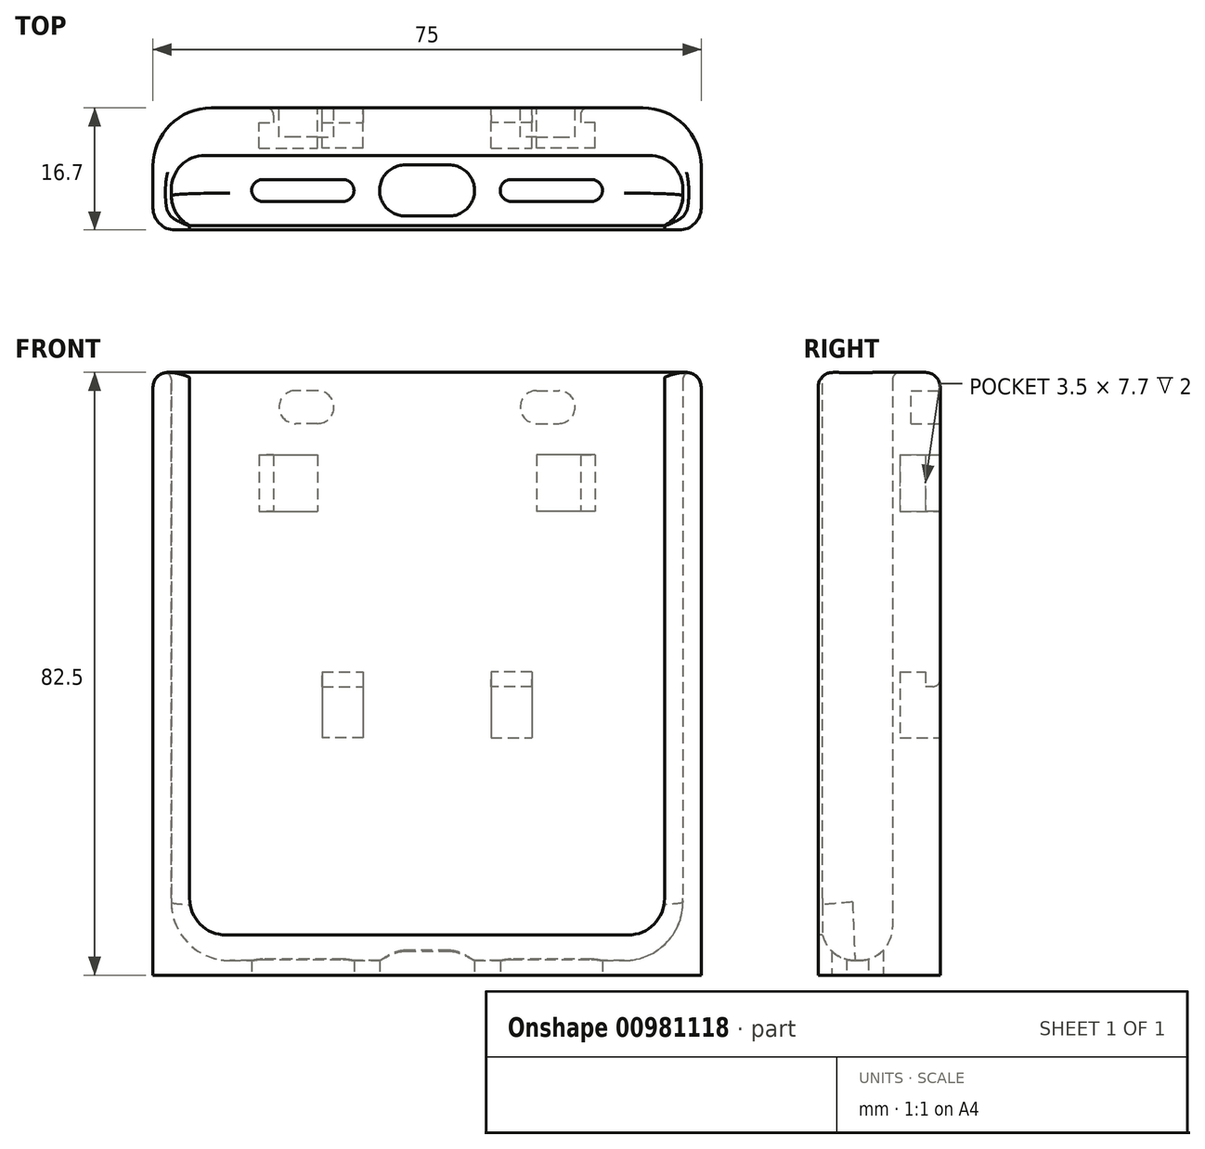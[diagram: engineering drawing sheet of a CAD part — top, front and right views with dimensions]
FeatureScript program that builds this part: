
annotation { "Feature Type Name" : "Feature", "Feature Type Description" : "" }
export const myFeature = defineFeature(function(context is Context, id is Id, definition is map)
    precondition{}
    {
        {
            var Q0;
            Q0=qCreatedBy(makeId("Front.planeOp"),FACE);
            var sketch = newSketch(context, id + "F0", { "sketchPlane" : qUnion([Q0])});
            skLineSegment(sketch, "E0", {"start": v(0, -32.88) * mm, "end": v(0, 44.67) * mm, "construction": true});
            skLineSegment(sketch, "E1.bottom", {"start": v(-23, 39.76) * mm, "end": v(-15, 39.76) * mm});
            skLineSegment(sketch, "E1.top", {"start": v(-23, 32.06) * mm, "end": v(-15, 32.06) * mm});
            skLineSegment(sketch, "E1.left", {"start": v(-23, 39.76) * mm, "end": v(-23, 32.06) * mm});
            skLineSegment(sketch, "E1.right", {"start": v(-15, 39.76) * mm, "end": v(-15, 32.06) * mm});
            skLineSegment(sketch, "E2.bottom", {"start": v(-8.75, 10.06) * mm, "end": v(-14.35, 10.06) * mm});
            skLineSegment(sketch, "E2.top", {"start": v(-8.75, 1.06) * mm, "end": v(-14.35, 1.06) * mm});
            skLineSegment(sketch, "E2.left", {"start": v(-8.75, 10.06) * mm, "end": v(-8.75, 1.06) * mm});
            skLineSegment(sketch, "E2.right", {"start": v(-14.35, 10.06) * mm, "end": v(-14.35, 1.06) * mm});
            skLineSegment(sketch, "E3.MirrorCS", {"start": v(15, 39.76) * mm, "end": v(15, 32.06) * mm});
            skLineSegment(sketch, "E4.MirrorCS", {"start": v(23, 32.06) * mm, "end": v(15, 32.06) * mm});
            skLineSegment(sketch, "E5.MirrorCS", {"start": v(23, 39.76) * mm, "end": v(23, 32.06) * mm});
            skLineSegment(sketch, "E6.MirrorCS", {"start": v(23, 39.76) * mm, "end": v(15, 39.76) * mm});
            skLineSegment(sketch, "E7.MirrorCS", {"start": v(8.75, 10.06) * mm, "end": v(14.35, 10.06) * mm});
            skLineSegment(sketch, "E8.MirrorCS", {"start": v(8.75, 10.06) * mm, "end": v(8.75, 1.06) * mm});
            skLineSegment(sketch, "E9.MirrorCS", {"start": v(8.75, 1.06) * mm, "end": v(14.35, 1.06) * mm});
            skLineSegment(sketch, "E10.MirrorCS", {"start": v(14.35, 10.06) * mm, "end": v(14.35, 1.06) * mm});
            skSolve(sketch);
        }
        {
            var Q0;
            Q0=qCreatedBy(makeId("Front.planeOp"),FACE);
            var sketch = newSketch(context, id + "F1", { "sketchPlane" : qUnion([Q0])});
            skLineSegment(sketch, "E11", {"start": v(0, -37.74) * mm, "end": v(0, 51.46) * mm, "construction": true});
            skLineSegment(sketch, "E12.bottom", {"start": v(0, 51.06) * mm, "end": v(-35, 51.06) * mm});
            skLineSegment(sketch, "E12.top", {"start": v(0, -28.94) * mm, "end": v(-27, -28.94) * mm});
            skLineSegment(sketch, "E12.left", {"start": v(0, 51.06) * mm, "end": v(0, -28.94) * mm});
            skLineSegment(sketch, "E12.right", {"start": v(-35, 51.06) * mm, "end": v(-35, -20.94) * mm});
            skPoint(sketch, "E13.visualSharp", {"position": v(-35, -28.94) * mm});
            skArc(sketch, "E13.filletArc", {"start": v(-35, -20.94) * mm, "mid": v(-32.66, -26.6) * mm, "end": v(-27, -28.94) * mm});
            skSolve(sketch);
        }
        {
            var Q0;
            Q0=qCreatedBy(makeId("Front.planeOp"),FACE);
            var sketch = newSketch(context, id + "F2", { "sketchPlane" : qUnion([Q0])});
            skLineSegment(sketch, "E14.bottom", {"start": v(0, 51.06) * mm, "end": v(-37.5, 51.06) * mm});
            skLineSegment(sketch, "E14.top", {"start": v(0, -31.44) * mm, "end": v(-37.5, -31.44) * mm});
            skLineSegment(sketch, "E14.right", {"start": v(-37.5, 51.06) * mm, "end": v(-37.5, -31.44) * mm});
            skPoint(sketch, "E15.visualSharp", {"position": v(-37.5, -31.44) * mm});
            skLineSegment(sketch, "E15.filletArc", {"start": v(-37.5, -31.44) * mm, "end": v(-37.5, -31.44) * mm});
            skLineSegment(sketch, "E16.MirrorCS", {"start": v(0, 51.06) * mm, "end": v(37.5, 51.06) * mm});
            skLineSegment(sketch, "E17.MirrorCS", {"start": v(37.5, 51.06) * mm, "end": v(37.5, -31.44) * mm});
            skLineSegment(sketch, "E18.MirrorCS", {"start": v(37.5, -31.44) * mm, "end": v(37.5, -31.44) * mm});
            skLineSegment(sketch, "E19.MirrorCS", {"start": v(0, -31.44) * mm, "end": v(37.5, -31.44) * mm});
            skSolve(sketch);
        }
        {
            var Q0;
            Q0 = qSketchRegion(id + "F2", true);
            extrude(context, id + "F3", {"entities" : qUnion([Q0]), "depth" : 16.7 * mm, "offsetDistance" : 25 * mm});
        }
        {
            var Q0;
            Q0 = qSketchRegion(id + "F0", true);
            extrude(context, id + "F4", {"entities" : qUnion([Q0]), "operationType" : NewBodyOperationType.REMOVE, "depth" : 5.5 * mm, "offsetDistance" : 25 * mm});
        }
        {
            var Q0;
            Q0=qCreatedBy(makeId("Front.planeOp"),FACE);
            cPlane(context, id + "F5", {"entities" : qUnion([Q0]), "cplaneType" : CPlaneType.OFFSET, "offset" : 6.5 * mm, "width" : 150 * mm, "height" : 150 * mm});
        }
        {
            var Q0;
            Q0=qCreatedBy(id+"F5.planeOp",FACE);
            var sketch = newSketch(context, id + "F6", { "sketchPlane" : qUnion([Q0])});
            skLineSegment(sketch, "E20", {"start": v(0, -47.03) * mm, "end": v(0, 63.52) * mm, "construction": true});
            skLineSegment(sketch, "E21.right", {"start": v(0, 51.73) * mm, "end": v(0, 51.06) * mm, "construction": true});
            skLineSegment(sketch, "E22.bottom", {"start": v(-35, 51.06) * mm, "end": v(0, 51.06) * mm});
            skLineSegment(sketch, "E22.top", {"start": v(-27, -29.44) * mm, "end": v(0, -29.44) * mm});
            skLineSegment(sketch, "E22.left", {"start": v(-35, 51.06) * mm, "end": v(-35, -21.44) * mm});
            skLineSegment(sketch, "E22.right", {"start": v(0, 51.06) * mm, "end": v(0, -29.44) * mm});
            skPoint(sketch, "E23.visualSharp", {"position": v(-35, -29.44) * mm});
            skArc(sketch, "E23.filletArc", {"start": v(-35, -21.44) * mm, "mid": v(-32.66, -27.1) * mm, "end": v(-27, -29.44) * mm});
            skLineSegment(sketch, "E24.MirrorCS", {"start": v(27, -29.44) * mm, "end": v(0, -29.44) * mm});
            skArc(sketch, "E25.MirrorCS", {"start": v(35, -21.44) * mm, "mid": v(32.66, -27.1) * mm, "end": v(27, -29.44) * mm});
            skLineSegment(sketch, "E26.MirrorCS", {"start": v(35, 51.06) * mm, "end": v(35, -21.44) * mm});
            skLineSegment(sketch, "E27.MirrorCS", {"start": v(35, 51.06) * mm, "end": v(0, 51.06) * mm});
            skSolve(sketch);
        }
        {
            var Q0;
            Q0 = qSketchRegion(id + "F6", true);
            extrude(context, id + "F7", {"entities" : qUnion([Q0]), "operationType" : NewBodyOperationType.REMOVE, "depth" : 9.6 * mm, "offsetDistance" : 25 * mm});
        }
        {
            var Q0;
            Q0=makeQuery(id+"F3.opExtrude","CAP_FACE",FACE,{"disambiguationData":[OSD([sQuery(id+"F2.wireOp",EDGE,"E14.bottom"),sQuery(id+"F2.wireOp",EDGE,"E14.top"),sQuery(id+"F2.wireOp",EDGE,"E14.right"),sQuery(id+"F2.wireOp",EDGE,"E15.filletArc"),sQuery(id+"F2.wireOp",EDGE,"E16.MirrorCS"),sQuery(id+"F2.wireOp",EDGE,"E17.MirrorCS"),sQuery(id+"F2.wireOp",EDGE,"E18.MirrorCS"),sQuery(id+"F2.wireOp",EDGE,"E19.MirrorCS")])],"isStart":false});
            var sketch = newSketch(context, id + "F8", { "sketchPlane" : qUnion([Q0])});
            skLineSegment(sketch, "E28", {"start": v(0, 61.95) * mm, "end": v(0, 51.06) * mm, "construction": true});
            skLineSegment(sketch, "E29.bottom", {"start": v(-32.5, 51.06) * mm, "end": v(0, 51.06) * mm});
            skLineSegment(sketch, "E29.top", {"start": v(-27.5, -25.94) * mm, "end": v(0, -25.94) * mm});
            skLineSegment(sketch, "E29.left", {"start": v(-32.5, 51.06) * mm, "end": v(-32.5, -20.94) * mm});
            skPoint(sketch, "E30.visualSharp", {"position": v(-32.5, -25.94) * mm});
            skArc(sketch, "E30.filletArc", {"start": v(-32.5, -20.94) * mm, "mid": v(-31.04, -24.48) * mm, "end": v(-27.5, -25.94) * mm});
            skLineSegment(sketch, "E31.trimOffspring", {"start": v(0, -25.94) * mm, "end": v(0, -47.05) * mm, "construction": true});
            skLineSegment(sketch, "E32.MirrorCS", {"start": v(27.5, -25.94) * mm, "end": v(0, -25.94) * mm});
            skArc(sketch, "E33.MirrorCS", {"start": v(32.5, -20.94) * mm, "mid": v(31.04, -24.48) * mm, "end": v(27.5, -25.94) * mm});
            skLineSegment(sketch, "E34.MirrorCS", {"start": v(32.5, 51.06) * mm, "end": v(32.5, -20.94) * mm});
            skLineSegment(sketch, "E35.MirrorCS", {"start": v(32.5, 51.06) * mm, "end": v(0, 51.06) * mm});
            skSolve(sketch);
        }
        {
            var Q0;
            Q0 = qSketchRegion(id + "F8", true);
            extrude(context, id + "F9", {"entities" : qUnion([Q0]), "operationType" : NewBodyOperationType.REMOVE, "endBound" : BoundingType.UP_TO_NEXT, "oppositeDirection" : true, "depth" : 25 * mm, "offsetDistance" : 25 * mm});
        }
        {
            var Q0;
            Q0=makeQuery(id+"F7.boolean.opBoolean","COPY",EDGE,{"derivedFrom":makeQuery(id+"F7.opExtrude","CAP_EDGE",EDGE,{"disambiguationData":[OSD([sQuery(id+"F6.wireOp",EDGE,"E22.left")])],"isStart":true})});
            fillet(context, id + "F10", {"entities" : qUnion([Q0]), "radius" : 4.6 * mm, "tangentPropagation" : true, "allowEdgeOverflow" : false});
        }
        {
            var Q0;
            Q0=makeQuery(id+"F7.boolean.opBoolean","COPY",EDGE,{"derivedFrom":makeQuery(id+"F7.opExtrude","CAP_EDGE",EDGE,{"disambiguationData":[OSD([sQuery(id+"F6.wireOp",EDGE,"E22.left")])],"isStart":false})});
            fillet(context, id + "F11", {"entities" : qUnion([Q0]), "radius" : 4.6 * mm, "tangentPropagation" : true, "allowEdgeOverflow" : false});
        }
        {
            var Q0;
            Q0=makeQuery(id+"F11.opFillet","BLEND_EDGE",EDGE,{"blendedFrom":[makeQuery(id+"F7.boolean.opBoolean","COPY",EDGE,{"derivedFrom":makeQuery(id+"F7.opExtrude","CAP_EDGE",EDGE,{"disambiguationData":[OSD([sQuery(id+"F6.wireOp",EDGE,"E26.MirrorCS")])],"isStart":false})}),makeQuery(id+"F3.opExtrude","SWEPT_FACE",FACE,{"disambiguationData":[OSD([sQuery(id+"F2.wireOp",EDGE,"E14.bottom"),sQuery(id+"F2.wireOp",EDGE,"E16.MirrorCS")])]})],"blendedInto":[makeQuery(id+"F3.opExtrude","SWEPT_FACE",FACE,{"disambiguationData":[OSD([sQuery(id+"F2.wireOp",EDGE,"E14.bottom"),sQuery(id+"F2.wireOp",EDGE,"E16.MirrorCS")])]})]});
            var Q1;
            {var subQ0=sQuery(id+"F6.wireOp",EDGE,"E27.MirrorCS");var subQ1=sQuery(id+"F6.wireOp",EDGE,"E26.MirrorCS");var subQ2=sQuery(id+"F6.wireOp",EDGE,"E22.bottom");Q1=makeQuery(id+"F9.boolean.opBoolean","SPLIT",EDGE,{"disambiguationData":[TD([makeQuery(id+"F7.boolean.opBoolean","COPY",FACE,{"derivedFrom":makeQuery(id+"F7.opExtrude","SWEPT_FACE",FACE,{"disambiguationData":[OSD([subQ1])]})})])],"derivedFrom":makeQuery(id+"F7.boolean.opBoolean","COPY",EDGE,{"derivedFrom":makeQuery(id+"F7.opExtrude","CAP_EDGE",EDGE,{"disambiguationData":[OSD([subQ2,subQ0])],"isStart":false})})});}
            fillet(context, id + "F12", {"entities" : qUnion([Q0, Q1]), "radius" : 1 * mm, "tangentPropagation" : true, "allowEdgeOverflow" : false});
        }
        {
            var Q0;
            Q0=makeQuery(id+"F4.boolean.opBoolean","COPY",FACE,{"derivedFrom":makeQuery(id+"F4.opExtrude","SWEPT_FACE",FACE,{"disambiguationData":[OSD([sQuery(id+"F0.wireOp",EDGE,"E4.MirrorCS")])]})});
            var sketch = newSketch(context, id + "F13", { "sketchPlane" : qUnion([Q0])});
            skLineSegment(sketch, "E36.bottom", {"start": v(23, 0) * mm, "end": v(22, 0) * mm});
            skLineSegment(sketch, "E36.top", {"start": v(23, -2) * mm, "end": v(21, -2) * mm});
            skLineSegment(sketch, "E36.left", {"start": v(23, 0) * mm, "end": v(23, -2) * mm});
            skLineSegment(sketch, "E36.right", {"start": v(21, -1) * mm, "end": v(21, -2) * mm});
            skPoint(sketch, "E37.visualSharp", {"position": v(21, 0) * mm});
            skArc(sketch, "E37.filletArc", {"start": v(22, 0) * mm, "mid": v(21.3, -0.3) * mm, "end": v(21, -1) * mm});
            skSolve(sketch);
        }
        {
            var Q0;
            Q0 = qSketchRegion(id + "F13", true);
            extrude(context, id + "F14", {"entities" : qUnion([Q0]), "operationType" : NewBodyOperationType.ADD, "endBound" : BoundingType.UP_TO_NEXT, "depth" : 25 * mm, "offsetDistance" : 25 * mm});
        }
        {
            var Q0;
            Q0=makeQuery(id+"F4.boolean.opBoolean","COPY",FACE,{"derivedFrom":makeQuery(id+"F4.opExtrude","SWEPT_FACE",FACE,{"disambiguationData":[OSD([sQuery(id+"F0.wireOp",EDGE,"E1.top")])]})});
            var sketch = newSketch(context, id + "F15", { "sketchPlane" : qUnion([Q0])});
            skLineSegment(sketch, "E38.bottom", {"start": v(-23, 0) * mm, "end": v(-22, 0) * mm});
            skLineSegment(sketch, "E38.top", {"start": v(-23, -2) * mm, "end": v(-21, -2) * mm});
            skLineSegment(sketch, "E38.left", {"start": v(-23, 0) * mm, "end": v(-23, -2) * mm});
            skLineSegment(sketch, "E38.right", {"start": v(-21, -1) * mm, "end": v(-21, -2) * mm});
            skPoint(sketch, "E39.visualSharp", {"position": v(-21, 0) * mm});
            skArc(sketch, "E39.filletArc", {"start": v(-21, -1) * mm, "mid": v(-21.3, -0.3) * mm, "end": v(-22, 0) * mm});
            skSolve(sketch);
        }
        {
            var Q0;
            Q0 = qSketchRegion(id + "F15", true);
            extrude(context, id + "F16", {"entities" : qUnion([Q0]), "operationType" : NewBodyOperationType.ADD, "endBound" : BoundingType.UP_TO_NEXT, "depth" : 25 * mm, "offsetDistance" : 25 * mm});
        }
        {
            var Q0;
            Q0=makeQuery(id+"F4.boolean.opBoolean","COPY",FACE,{"derivedFrom":makeQuery(id+"F4.opExtrude","SWEPT_FACE",FACE,{"disambiguationData":[OSD([sQuery(id+"F0.wireOp",EDGE,"E2.left")])]})});
            var sketch = newSketch(context, id + "F17", { "sketchPlane" : qUnion([Q0])});
            skLineSegment(sketch, "E40.bottom", {"start": v(0, 10.06) * mm, "end": v(2, 10.06) * mm});
            skLineSegment(sketch, "E40.top", {"start": v(1, 8.06) * mm, "end": v(2, 8.06) * mm});
            skLineSegment(sketch, "E40.left", {"start": v(0, 10.06) * mm, "end": v(0, 9.06) * mm});
            skLineSegment(sketch, "E40.right", {"start": v(2, 10.06) * mm, "end": v(2, 8.06) * mm});
            skPoint(sketch, "E41.visualSharp", {"position": v(0, 8.06) * mm});
            skArc(sketch, "E41.filletArc", {"start": v(0, 9.06) * mm, "mid": v(0.3, 8.35) * mm, "end": v(1, 8.06) * mm});
            skSolve(sketch);
        }
        {
            var Q0;
            Q0 = qSketchRegion(id + "F17", true);
            extrude(context, id + "F18", {"entities" : qUnion([Q0]), "operationType" : NewBodyOperationType.ADD, "endBound" : BoundingType.UP_TO_NEXT, "depth" : 25 * mm, "offsetDistance" : 25 * mm});
        }
        {
            var Q0;
            Q0=makeQuery(id+"F4.boolean.opBoolean","COPY",FACE,{"derivedFrom":makeQuery(id+"F4.opExtrude","SWEPT_FACE",FACE,{"disambiguationData":[OSD([sQuery(id+"F0.wireOp",EDGE,"E8.MirrorCS")])]})});
            var sketch = newSketch(context, id + "F19", { "sketchPlane" : qUnion([Q0])});
            skLineSegment(sketch, "E42.bottom", {"start": v(0, 10.06) * mm, "end": v(-2, 10.06) * mm});
            skLineSegment(sketch, "E42.top", {"start": v(-1, 8.06) * mm, "end": v(-2, 8.06) * mm});
            skLineSegment(sketch, "E42.left", {"start": v(0, 10.06) * mm, "end": v(0, 9.06) * mm});
            skLineSegment(sketch, "E42.right", {"start": v(-2, 10.06) * mm, "end": v(-2, 8.06) * mm});
            skPoint(sketch, "E43.visualSharp", {"position": v(0, 8.06) * mm});
            skArc(sketch, "E43.filletArc", {"start": v(-1, 8.06) * mm, "mid": v(-0.3, 8.35) * mm, "end": v(0, 9.06) * mm});
            skSolve(sketch);
        }
        {
            var Q0;
            Q0 = qSketchRegion(id + "F19", true);
            extrude(context, id + "F20", {"entities" : qUnion([Q0]), "operationType" : NewBodyOperationType.ADD, "endBound" : BoundingType.UP_TO_NEXT, "depth" : 25 * mm, "offsetDistance" : 25 * mm});
        }
        {
            var Q0;
            Q0=makeQuery(id+"F3.opExtrude","SWEPT_FACE",FACE,{"disambiguationData":[OSD([sQuery(id+"F2.wireOp",EDGE,"E14.top"),sQuery(id+"F2.wireOp",EDGE,"E19.MirrorCS")])]});
            var sketch = newSketch(context, id + "F21", { "sketchPlane" : qUnion([Q0])});
            skLineSegment(sketch, "E44", {"start": v(-40.57, 11.3) * mm, "end": v(-17, 11.3) * mm, "construction": true});
            skLineSegment(sketch, "E45", {"start": v(0, 24.83) * mm, "end": v(0, 14.8) * mm, "construction": true});
            skLineSegment(sketch, "E46.bottom", {"start": v(-3, 14.8) * mm, "end": v(0, 14.8) * mm});
            skLineSegment(sketch, "E46.left", {"start": v(-6.5, 11.3) * mm, "end": v(-6.5, 11.3) * mm});
            skLineSegment(sketch, "E47.trimOffspring", {"start": v(0, 8.91) * mm, "end": v(0, -15.6) * mm, "construction": true});
            skPoint(sketch, "E48.visualSharp", {"position": v(-6.5, 14.8) * mm});
            skArc(sketch, "E48.filletArc", {"start": v(-3, 14.8) * mm, "mid": v(-5.47, 13.77) * mm, "end": v(-6.5, 11.3) * mm});
            skArc(sketch, "E49.MirrorCS", {"start": v(-3, 7.8) * mm, "mid": v(-5.47, 8.83) * mm, "end": v(-6.5, 11.3) * mm});
            skLineSegment(sketch, "E50.MirrorCS", {"start": v(-3, 7.8) * mm, "end": v(0, 7.8) * mm});
            skLineSegment(sketch, "E51.MirrorCS", {"start": v(3, 14.8) * mm, "end": v(0, 14.8) * mm});
            skArc(sketch, "E52.MirrorCS", {"start": v(3, 14.8) * mm, "mid": v(5.47, 13.77) * mm, "end": v(6.5, 11.3) * mm});
            skArc(sketch, "E53.MirrorCS", {"start": v(3, 7.8) * mm, "mid": v(5.47, 8.83) * mm, "end": v(6.5, 11.3) * mm});
            skLineSegment(sketch, "E54.MirrorCS", {"start": v(3, 7.8) * mm, "end": v(0, 7.8) * mm});
            skLineSegment(sketch, "E55", {"start": v(-17, 21.85) * mm, "end": v(-17, 12.8) * mm, "construction": true});
            skLineSegment(sketch, "E56.top", {"start": v(-17, 12.8) * mm, "end": v(-22.5, 12.8) * mm});
            skPoint(sketch, "E57.visualSharp", {"position": v(-24, 12.8) * mm});
            skArc(sketch, "E57.filletArc", {"start": v(-22.5, 12.8) * mm, "mid": v(-23.56, 12.36) * mm, "end": v(-24, 11.3) * mm});
            skLineSegment(sketch, "E58.trimOffspring", {"start": v(-17, 11.3) * mm, "end": v(-17, -5.52) * mm, "construction": true});
            skLineSegment(sketch, "E59.trimOffspring", {"start": v(-17, 11.3) * mm, "end": v(38.86, 11.3) * mm, "construction": true});
            skArc(sketch, "E60.MirrorCS", {"start": v(-22.5, 9.8) * mm, "mid": v(-23.56, 10.24) * mm, "end": v(-24, 11.3) * mm});
            skLineSegment(sketch, "E61.MirrorCS", {"start": v(-17, 9.8) * mm, "end": v(-22.5, 9.8) * mm});
            skLineSegment(sketch, "E62.MirrorCS", {"start": v(-17, 12.8) * mm, "end": v(-11.5, 12.8) * mm});
            skArc(sketch, "E63.MirrorCS", {"start": v(-11.5, 12.8) * mm, "mid": v(-10.44, 12.36) * mm, "end": v(-10, 11.3) * mm});
            skArc(sketch, "E64.MirrorCS", {"start": v(-11.5, 9.8) * mm, "mid": v(-10.44, 10.24) * mm, "end": v(-10, 11.3) * mm});
            skLineSegment(sketch, "E65.MirrorCS", {"start": v(-17, 9.8) * mm, "end": v(-11.5, 9.8) * mm});
            skArc(sketch, "E66.MirrorCS", {"start": v(11.5, 9.8) * mm, "mid": v(10.44, 10.24) * mm, "end": v(10, 11.3) * mm});
            skArc(sketch, "E67.MirrorCS", {"start": v(11.5, 12.8) * mm, "mid": v(10.44, 12.36) * mm, "end": v(10, 11.3) * mm});
            skLineSegment(sketch, "E68.MirrorCS", {"start": v(17, 12.8) * mm, "end": v(11.5, 12.8) * mm});
            skLineSegment(sketch, "E69.MirrorCS", {"start": v(17, 9.8) * mm, "end": v(11.5, 9.8) * mm});
            skLineSegment(sketch, "E70.MirrorCS", {"start": v(17, 9.8) * mm, "end": v(22.5, 9.8) * mm});
            skArc(sketch, "E71.MirrorCS", {"start": v(22.5, 9.8) * mm, "mid": v(23.56, 10.24) * mm, "end": v(24, 11.3) * mm});
            skArc(sketch, "E72.MirrorCS", {"start": v(22.5, 12.8) * mm, "mid": v(23.56, 12.36) * mm, "end": v(24, 11.3) * mm});
            skLineSegment(sketch, "E73.MirrorCS", {"start": v(17, 12.8) * mm, "end": v(22.5, 12.8) * mm});
            skSolve(sketch);
        }
        {
            var Q0;
            Q0 = qSketchRegion(id + "F21", true);
            extrude(context, id + "F22", {"entities" : qUnion([Q0]), "operationType" : NewBodyOperationType.REMOVE, "endBound" : BoundingType.UP_TO_NEXT, "oppositeDirection" : true, "depth" : 25 * mm, "offsetDistance" : 25 * mm});
        }
        {
            var Q0;
            Q0=makeQuery(id+"F3.opExtrude","CAP_EDGE",EDGE,{"disambiguationData":[OSD([sQuery(id+"F2.wireOp",EDGE,"E14.right")])],"isStart":true});
            var Q1;
            Q1=makeQuery(id+"F3.opExtrude","CAP_EDGE",EDGE,{"disambiguationData":[OSD([sQuery(id+"F2.wireOp",EDGE,"E17.MirrorCS")])],"isStart":true});
            fillet(context, id + "F23", {"entities" : qUnion([Q0, Q1]), "radius" : 8 * mm, "tangentPropagation" : true, "allowEdgeOverflow" : false});
        }
        {
            var Q0;
            Q0=makeQuery(id+"F3.opExtrude","CAP_EDGE",EDGE,{"disambiguationData":[OSD([sQuery(id+"F2.wireOp",EDGE,"E14.right")])],"isStart":false});
            var Q1;
            Q1=makeQuery(id+"F3.opExtrude","CAP_EDGE",EDGE,{"disambiguationData":[OSD([sQuery(id+"F2.wireOp",EDGE,"E17.MirrorCS")])],"isStart":false});
            fillet(context, id + "F24", {"entities" : qUnion([Q0, Q1]), "radius" : 3 * mm, "tangentPropagation" : true, "allowEdgeOverflow" : false});
        }
        {
            var Q0;
            Q0=makeQuery(id+"F24.opFillet","BLEND_EDGE",EDGE,{"blendedFrom":[makeQuery(id+"F3.opExtrude","CAP_EDGE",EDGE,{"disambiguationData":[OSD([sQuery(id+"F2.wireOp",EDGE,"E14.right")])],"isStart":false}),makeQuery(id+"F3.opExtrude","SWEPT_FACE",FACE,{"disambiguationData":[OSD([sQuery(id+"F2.wireOp",EDGE,"E14.bottom"),sQuery(id+"F2.wireOp",EDGE,"E16.MirrorCS")])]})],"blendedInto":[makeQuery(id+"F3.opExtrude","SWEPT_FACE",FACE,{"disambiguationData":[OSD([sQuery(id+"F2.wireOp",EDGE,"E14.bottom"),sQuery(id+"F2.wireOp",EDGE,"E16.MirrorCS")])]})]});
            fillet(context, id + "F25", {"entities" : qUnion([Q0]), "radius" : 2 * mm, "tangentPropagation" : true, "allowEdgeOverflow" : false});
        }
        {
            var Q0;
            Q0=makeQuery(id+"F20.boolean.opBoolean","MERGE",FACE,{"derivedFrom":[makeQuery(id+"F18.boolean.opBoolean","MERGE",FACE,{"derivedFrom":[makeQuery(id+"F16.boolean.opBoolean","MERGE",FACE,{"derivedFrom":[makeQuery(id+"F14.boolean.opBoolean","MERGE",FACE,{"derivedFrom":[makeQuery(id+"F3.opExtrude","CAP_FACE",FACE,{"disambiguationData":[OSD([sQuery(id+"F2.wireOp",EDGE,"E14.bottom"),sQuery(id+"F2.wireOp",EDGE,"E14.top"),sQuery(id+"F2.wireOp",EDGE,"E14.right"),sQuery(id+"F2.wireOp",EDGE,"E16.MirrorCS"),sQuery(id+"F2.wireOp",EDGE,"E17.MirrorCS"),sQuery(id+"F2.wireOp",EDGE,"E19.MirrorCS")])],"isStart":true}),makeQuery(id+"F14.opExtrude","SWEPT_FACE",FACE,{"disambiguationData":[OSD([sQuery(id+"F13.wireOp",EDGE,"E36.bottom")])]})]}),makeQuery(id+"F16.opExtrude","SWEPT_FACE",FACE,{"disambiguationData":[OSD([sQuery(id+"F15.wireOp",EDGE,"E38.bottom")])]})]}),makeQuery(id+"F18.opExtrude","SWEPT_FACE",FACE,{"disambiguationData":[OSD([sQuery(id+"F17.wireOp",EDGE,"E40.left")])]})]}),makeQuery(id+"F20.opExtrude","SWEPT_FACE",FACE,{"disambiguationData":[OSD([sQuery(id+"F19.wireOp",EDGE,"E42.left")])]})]});
            var sketch = newSketch(context, id + "F26", { "sketchPlane" : qUnion([Q0])});
            skLineSegment(sketch, "E74", {"start": v(0, 68.54) * mm, "end": v(0, -55.98) * mm, "construction": true});
            skArc(sketch, "E75", {"start": v(15, 48.56) * mm, "mid": v(12.75, 46.3) * mm, "end": v(15, 44.06) * mm});
            skArc(sketch, "E76", {"start": v(18, 44.06) * mm, "mid": v(20.25, 46.3) * mm, "end": v(18, 48.56) * mm});
            skLineSegment(sketch, "E77", {"start": v(15, 48.56) * mm, "end": v(18, 48.56) * mm});
            skLineSegment(sketch, "E78", {"start": v(15, 44.06) * mm, "end": v(18, 44.06) * mm});
            skArc(sketch, "E79.MirrorCS", {"start": v(-15, 48.56) * mm, "mid": v(-12.75, 46.3) * mm, "end": v(-15, 44.06) * mm});
            skLineSegment(sketch, "E80.MirrorCS", {"start": v(-15, 48.56) * mm, "end": v(-18, 48.56) * mm});
            skLineSegment(sketch, "E81.MirrorCS", {"start": v(-15, 44.06) * mm, "end": v(-18, 44.06) * mm});
            skArc(sketch, "E82.MirrorCS", {"start": v(-18, 44.06) * mm, "mid": v(-20.25, 46.3) * mm, "end": v(-18, 48.56) * mm});
            skSolve(sketch);
        }
        {
            var Q0;
            Q0 = qSketchRegion(id + "F26", true);
            extrude(context, id + "F27", {"entities" : qUnion([Q0]), "operationType" : NewBodyOperationType.REMOVE, "oppositeDirection" : true, "depth" : 4 * mm, "offsetDistance" : 25 * mm});
        }
    });
